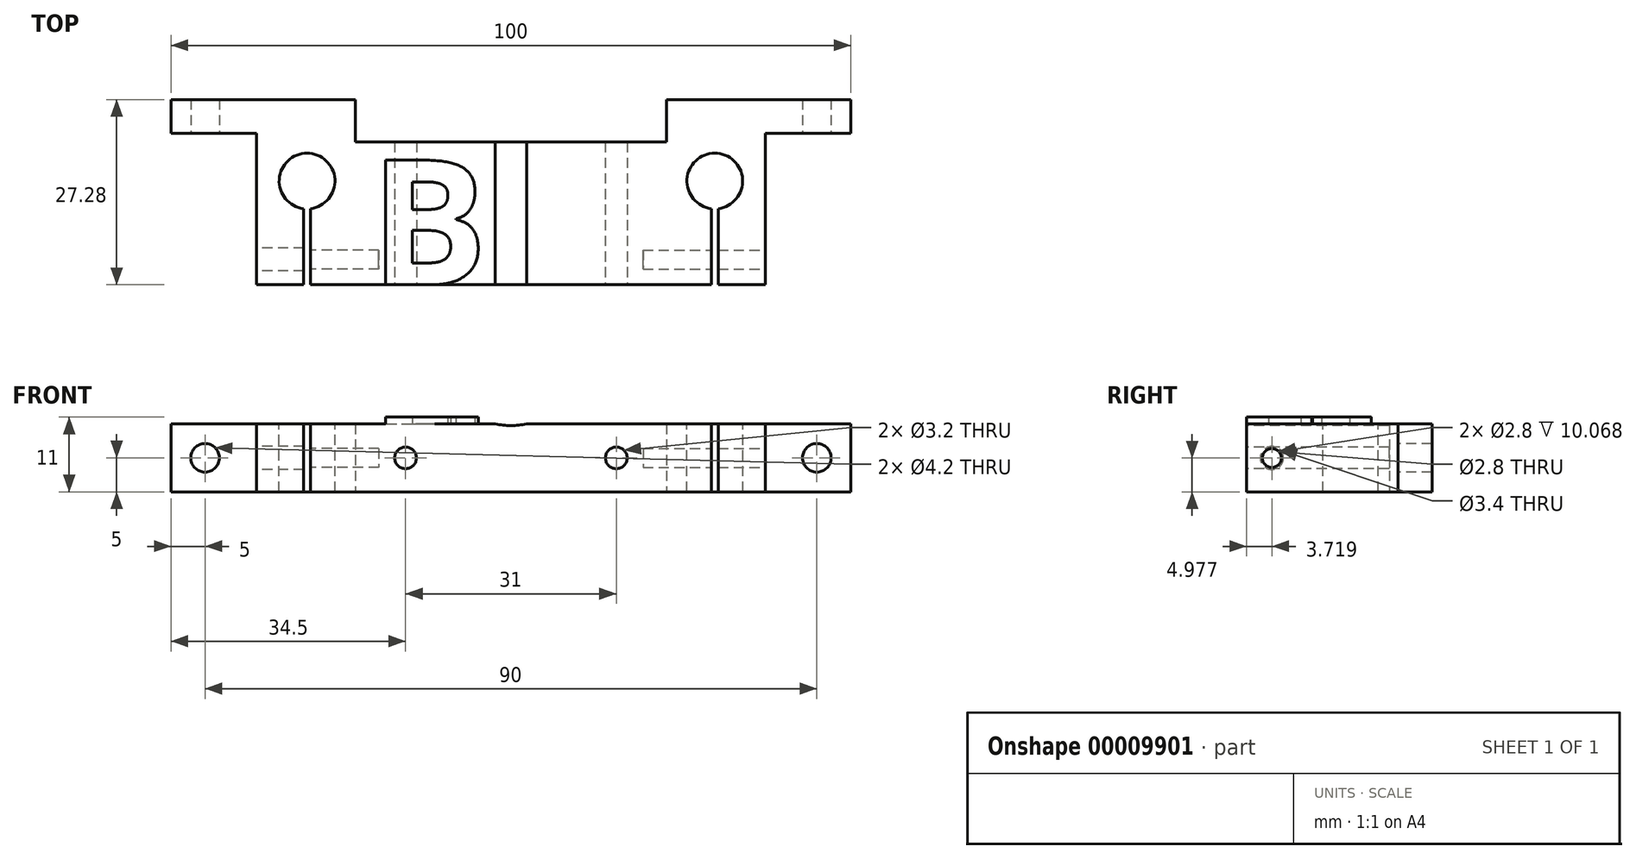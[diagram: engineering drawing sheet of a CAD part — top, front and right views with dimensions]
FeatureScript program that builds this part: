
annotation { "Feature Type Name" : "Feature", "Feature Type Description" : "" }
export const myFeature = defineFeature(function(context is Context, id is Id, definition is map)
    precondition{}
    {
        {
            var Q0;
            Q0=qCreatedBy(makeId("Top.planeOp"),FACE);
            var sketch = newSketch(context, id + "F0", { "sketchPlane" : qUnion([Q0])});
            skLineSegment(sketch, "E0", {"start": v(0, -13.82) * mm, "end": v(-37.44, -13.82) * mm});
            skLineSegment(sketch, "E1", {"start": v(-37.44, -13.82) * mm, "end": v(-37.44, 8.46) * mm});
            skLineSegment(sketch, "E2", {"start": v(-37.44, 8.46) * mm, "end": v(-50, 8.46) * mm});
            skLineSegment(sketch, "E3", {"start": v(-50, 8.46) * mm, "end": v(-50, 13.46) * mm});
            skLineSegment(sketch, "E4", {"start": v(-50, 13.46) * mm, "end": v(-22.87, 13.46) * mm});
            skLineSegment(sketch, "E5", {"start": v(-22.87, 13.46) * mm, "end": v(-22.87, 7.18) * mm});
            skLineSegment(sketch, "E6", {"start": v(-22.87, 7.18) * mm, "end": v(0, 7.18) * mm});
            skLineSegment(sketch, "E7", {"start": v(0, 7.18) * mm, "end": v(0, -13.82) * mm});
            skSolve(sketch);
        }
        {
            var Q0;
            Q0 = qSketchRegion(id + "F0", true);
            extrude(context, id + "F1", {"entities" : qUnion([Q0]), "depth" : 10 * mm});
        }
        {
            var Q0;
            Q0=makeQuery(id+"F1.opExtrude","SWEPT_FACE",FACE,{"disambiguationData":[OSD([sQuery(id+"F0.wireOp",EDGE,"E0")])]});
            var sketch = newSketch(context, id + "F2", { "sketchPlane" : qUnion([Q0])});
            skLineSegment(sketch, "E8", {"start": v(0, 5) * mm, "end": v(0, 5) * mm});
            skCircle(sketch, "E9", {"center": v(-15.5, 5) * mm, "radius": 1.6 * mm});
            skCircle(sketch, "E10", {"center": v(0, 20.5) * mm, "radius": 10.75 * mm});
            skSolve(sketch);
        }
        {
            var Q0;
            Q0 = qSketchRegion(id + "F2", true);
            extrude(context, id + "F3", {"entities" : qUnion([Q0]), "operationType" : NewBodyOperationType.REMOVE, "endBound" : BoundingType.THROUGH_ALL, "oppositeDirection" : true, "depth" : 25 * mm});
        }
        {
            var Q0;
            Q0=makeQuery(id+"F1.opExtrude","SWEPT_FACE",FACE,{"disambiguationData":[OSD([sQuery(id+"F0.wireOp",EDGE,"E2")])]});
            var sketch = newSketch(context, id + "F4", { "sketchPlane" : qUnion([Q0])});
            skLineSegment(sketch, "E11", {"start": v(-50, 5) * mm, "end": v(-37.44, 5) * mm, "construction": true});
            skLineSegment(sketch, "E12", {"start": v(-43.72, 10) * mm, "end": v(-43.72, 0) * mm, "construction": true});
            skCircle(sketch, "E13", {"center": v(-45, 5) * mm, "radius": 2.1 * mm});
            skSolve(sketch);
        }
        {
            var Q0;
            Q0 = qSketchRegion(id + "F4", true);
            extrude(context, id + "F5", {"entities" : qUnion([Q0]), "operationType" : NewBodyOperationType.REMOVE, "endBound" : BoundingType.THROUGH_ALL, "oppositeDirection" : true, "depth" : 25 * mm});
        }
        {
            var Q0;
            {var subQ0=makeQuery(id+"F1.opExtrude","CAP_FACE",FACE,{"disambiguationData":[OSD([sQuery(id+"F0.wireOp",EDGE,"E0"),sQuery(id+"F0.wireOp",EDGE,"fd64a43a-5635-4f94-a977-4dd36923accb"),sQuery(id+"F0.wireOp",EDGE,"1334f7d4-4c90-4769-8fa3-fe5f576fb005"),sQuery(id+"F0.wireOp",EDGE,"E1"),sQuery(id+"F0.wireOp",EDGE,"E2"),sQuery(id+"F0.wireOp",EDGE,"E3"),sQuery(id+"F0.wireOp",EDGE,"E4"),sQuery(id+"F0.wireOp",EDGE,"E5"),sQuery(id+"F0.wireOp",EDGE,"E6"),sQuery(id+"F0.wireOp",EDGE,"E7")])],"isStart":false});Q0=makeQuery(id+"F10.boolean.opBoolean","MERGE",FACE,{"derivedFrom":[subQ0,makeQuery(id+"F10.opPattern","COPY",FACE,{"derivedFrom":subQ0,"instanceName":"1"})]});}
            var sketch = newSketch(context, id + "F6", { "sketchPlane" : qUnion([Q0])});
            skCircle(sketch, "E14", {"center": v(-30, 1.46) * mm, "radius": 4.1 * mm});
            skLineSegment(sketch, "E15", {"start": v(-30, 1.46) * mm, "end": v(-30, -13.82) * mm, "construction": true});
            skLineSegment(sketch, "E16.bottom", {"start": v(-30.49, -2.04) * mm, "end": v(-29.51, -2.04) * mm});
            skLineSegment(sketch, "E16.top", {"start": v(-30.49, -14.16) * mm, "end": v(-29.51, -14.16) * mm});
            skLineSegment(sketch, "E16.left", {"start": v(-30.49, -2.04) * mm, "end": v(-30.49, -14.16) * mm});
            skLineSegment(sketch, "E16.right", {"start": v(-29.51, -2.04) * mm, "end": v(-29.51, -14.16) * mm});
            skPoint(sketch, "E17", {"position": v(-30, -2.04) * mm});
            skSolve(sketch);
        }
        {
            var Q0;
            Q0 = qSketchRegion(id + "F6", true);
            var Q1;
            {var subQ3=sQuery(id+"F6.wireOp",EDGE,"E16.bottom");Q1=makeQuery(id+"F6.imprint","IMPRINT",FACE,{"disambiguationData":[TD([[makeQuery(id+"F6.imprint","IMPRINT",EDGE,{"derivedFrom":subQ3}),-1.0]])]});}
            extrude(context, id + "F7", {"entities" : qUnion([Q0, Q1]), "operationType" : NewBodyOperationType.REMOVE, "endBound" : BoundingType.THROUGH_ALL, "oppositeDirection" : true, "depth" : 25 * mm});
        }
        {
            var Q0;
            Q0=makeQuery(id+"F1.opExtrude","SWEPT_FACE",FACE,{"disambiguationData":[OSD([sQuery(id+"F0.wireOp",EDGE,"E1")])]});
            var sketch = newSketch(context, id + "F8", { "sketchPlane" : qUnion([Q0])});
            skCircle(sketch, "E18", {"center": v(10.1, 4.98) * mm, "radius": 1.4 * mm});
            skCircle(sketch, "E19", {"center": v(10.1, 4.98) * mm, "radius": 1.7 * mm});
            skSolve(sketch);
        }
        {
            var Q0;
            Q0=makeQuery(id+"F8.imprint","IMPRINT",FACE,{"disambiguationData":[TD([[makeQuery(id+"F8.imprint","IMPRINT",EDGE,{"derivedFrom":sQuery(id+"F8.wireOp",EDGE,"E18")}),1.0]])]});
            extrude(context, id + "F9", {"entities" : qUnion([Q0]), "operationType" : NewBodyOperationType.REMOVE, "oppositeDirection" : true, "depth" : 18 * mm});
        }
        {
            var Q0;
            Q0=makeQuery(id+"F1.opExtrude","SWEPT_BODY",BODY,{"disambiguationData":[OSD([sQuery(id+"F0.wireOp",EDGE,"E0"),sQuery(id+"F0.wireOp",EDGE,"fd64a43a-5635-4f94-a977-4dd36923accb"),sQuery(id+"F0.wireOp",EDGE,"1334f7d4-4c90-4769-8fa3-fe5f576fb005"),sQuery(id+"F0.wireOp",EDGE,"E1"),sQuery(id+"F0.wireOp",EDGE,"E2"),sQuery(id+"F0.wireOp",EDGE,"E3"),sQuery(id+"F0.wireOp",EDGE,"E4"),sQuery(id+"F0.wireOp",EDGE,"E5"),sQuery(id+"F0.wireOp",EDGE,"E6"),sQuery(id+"F0.wireOp",EDGE,"E7")])]});
            var Q1;
            Q1=qCreatedBy(makeId("Right.planeOp"),FACE);
            mirror(context, id + "F10", {"operationType" : NewBodyOperationType.ADD, "entities" : qUnion([Q0]), "mirrorPlane" : qUnion([Q1])});
        }
        {
            var Q0;
            Q0=makeQuery(id+"F1.opExtrude","CAP_FACE",FACE,{"disambiguationData":[OSD([sQuery(id+"F0.wireOp",EDGE,"E0"),sQuery(id+"F0.wireOp",EDGE,"E1"),sQuery(id+"F0.wireOp",EDGE,"E2"),sQuery(id+"F0.wireOp",EDGE,"E3"),sQuery(id+"F0.wireOp",EDGE,"E4"),sQuery(id+"F0.wireOp",EDGE,"E5"),sQuery(id+"F0.wireOp",EDGE,"E6"),sQuery(id+"F0.wireOp",EDGE,"E7")])],"isStart":false});
            var sketch = newSketch(context, id + "F11", { "sketchPlane" : qUnion([Q0])});
            skText(sketch, "E20", { "text": "B", "fontName": "OpenSans-Bold.ttf"});
            const initialGuessF11  = {"E20": [-0.02073, -0.01382, 1, 0, 0.0185]};
            skSetInitialGuess(sketch, initialGuessF11);
            skSolve(sketch);
        }
        {
            var Q0;
            Q0 = qSketchRegion(id + "F11", true);
            extrude(context, id + "F12", {"entities" : qUnion([Q0]), "operationType" : NewBodyOperationType.ADD, "depth" : 1 * mm});
        }
        {
            var Q0;
            Q0=makeQuery(id+"F8.imprint","IMPRINT",FACE,{"disambiguationData":[TD([[makeQuery(id+"F8.imprint","IMPRINT",EDGE,{"derivedFrom":sQuery(id+"F8.wireOp",EDGE,"E18")}),1.0]])]});
            var Q1;
            Q1=makeQuery(id+"F8.imprint","IMPRINT",FACE,{"disambiguationData":[TD([[makeQuery(id+"F8.imprint","IMPRINT",EDGE,{"derivedFrom":sQuery(id+"F8.wireOp",EDGE,"E18")}),-1.0]])]});
            extrude(context, id + "F13", {"entities" : qUnion([Q0, Q1]), "operationType" : NewBodyOperationType.REMOVE, "endBound" : BoundingType.UP_TO_NEXT, "oppositeDirection" : true, "depth" : 25 * mm});
        }
    });
